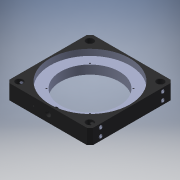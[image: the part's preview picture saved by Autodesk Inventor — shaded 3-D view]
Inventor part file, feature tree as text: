
AUTODESK INVENTOR PART (.ipt)
format: ipt  version: 2016 (Build 200138000, 138)  size: 410,624 bytes
history: native  units: mm
features: other x10, imported_body x9, sketch x3, extrude x2, projected_geometry x2, hole x1
ambient origin geometry x8: Origin, YZ Plane, XZ Plane, XY Plane, X Axis, Y Axis, Z Axis, Center Point
bodies: Body1 (feature_tree), Body2 (feature_tree), Body3 (feature_tree), Body4 (feature_tree), Body5 (feature_tree), Body6 (feature_tree), Body7 (feature_tree), Body8 (feature_tree), Body9 (feature_tree)
feature tree (27):
  other  "13108-001-1-solid1"
  other  "13108-E0W1"
  extrude  "Extrusion1"  Depth=5.25mm TaperAngle=0.0deg
  extrude  "Extrusion2"  Depth=4.0mm TaperAngle=0.0deg
  hole  "Hole1"  [1 undecoded]
  other  "SS4S019-1-1-solid1"
  other  "SS4S019-1-2-solid1"
  other  "SS4S019-1-3-solid1"
  other  "SS4S019-1-4-solid1"
  other  "SS4S019-1-5-solid1"
  other  "SS4S019-1-6-solid1"
  other  "SS4S019-1-7-solid1"
  other  "SS4S019-1-8-solid1"
  imported_body  "Base1"
  imported_body  "Base2"
  imported_body  "Base3"
  imported_body  "Base4"
  imported_body  "Base5"
  imported_body  "Base6"
  imported_body  "Base7"
  imported_body  "Base8"
  imported_body  "Base9"
  sketch  "Sketch1"  dims[d1=68.0mm d2=5.25mm d3=0.0mm]
  projected_geometry  "Projected Loop1"
  sketch  "Sketch2"  dims[d4=50.0mm d5=4.0mm d6=0.0mm]
  sketch  "Sketch3"  dims[d7=36.99764mm d8=36.99764mm d9=1.3208mm d10=3.4036mm d11=9.525mm d12=6.35mm d13=14.3117mm d14=5.5118mm d15=20.594885mm]
  projected_geometry  "Projected Loop2"
note: 1 required parameter value undecoded (feature->parameter linkage not recoverable at this tier; creation-order binding heuristic only, values carry confidence <= 0.55)
